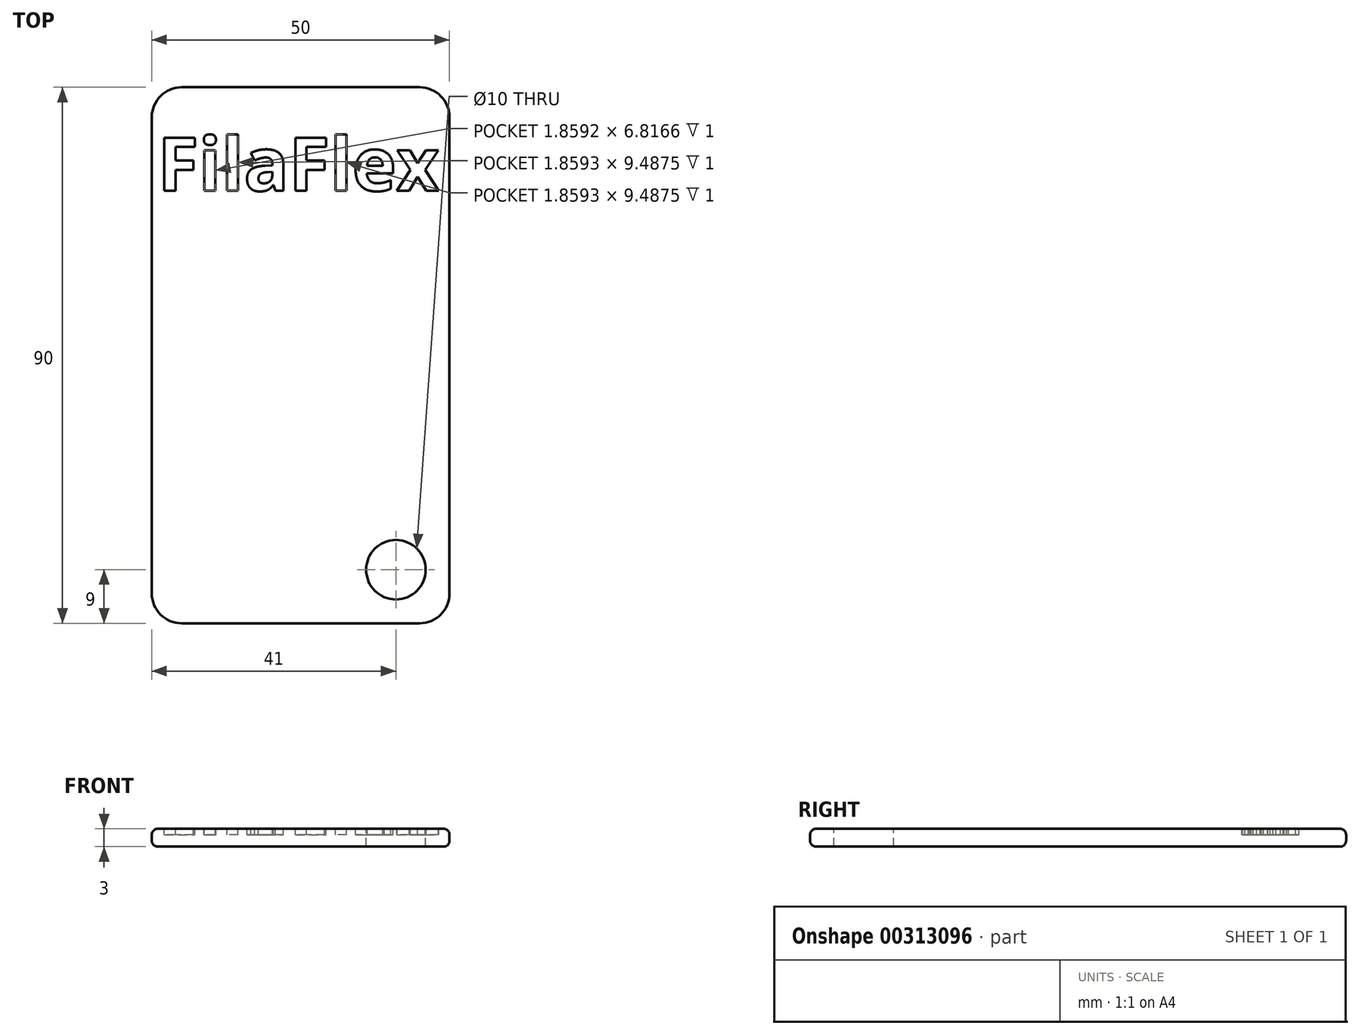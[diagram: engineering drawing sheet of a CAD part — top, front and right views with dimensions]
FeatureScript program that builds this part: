
annotation { "Feature Type Name" : "Feature", "Feature Type Description" : "" }
export const myFeature = defineFeature(function(context is Context, id is Id, definition is map)
    precondition{}
    {
        {
            var Q0;
            Q0=qCreatedBy(makeId("Top.planeOp"),FACE);
            var sketch = newSketch(context, id + "F0", { "sketchPlane" : qUnion([Q0])});
            skLineSegment(sketch, "E0.bottom", {"start": v(-45, 25) * mm, "end": v(45, 25) * mm});
            skLineSegment(sketch, "E0.top", {"start": v(-45, -25) * mm, "end": v(45, -25) * mm});
            skLineSegment(sketch, "E0.left", {"start": v(-45, 25) * mm, "end": v(-45, -25) * mm});
            skLineSegment(sketch, "E0.right", {"start": v(45, 25) * mm, "end": v(45, -25) * mm});
            skLineSegment(sketch, "E1", {"start": v(-45, 25) * mm, "end": v(45, -25) * mm, "construction": true});
            skSolve(sketch);
        }
        {
            var Q0;
            Q0=makeQuery(id+"F0.imprint","IMPRINT",FACE,{"disambiguationData":[TD([[makeQuery(id+"F0.imprint","IMPRINT",EDGE,{"derivedFrom":sQuery(id+"F0.wireOp",EDGE,"E0.bottom")}),-1.0]])]});
            extrude(context, id + "F1", {"entities" : qUnion([Q0]), "depth" : 3 * mm});
        }
        {
            var Q0;
            Q0=makeQuery(id+"F1.opExtrude","CAP_FACE",FACE,{"disambiguationData":[OSD([sQuery(id+"F0.wireOp",EDGE,"E0.bottom"),sQuery(id+"F0.wireOp",EDGE,"E0.top"),sQuery(id+"F0.wireOp",EDGE,"E0.left"),sQuery(id+"F0.wireOp",EDGE,"E0.right")])],"isStart":false});
            var Q1;
            Q1=makeQuery(id+"F1.opExtrude","CAP_FACE",FACE,{"disambiguationData":[OSD([sQuery(id+"F0.wireOp",EDGE,"E0.bottom"),sQuery(id+"F0.wireOp",EDGE,"E0.top"),sQuery(id+"F0.wireOp",EDGE,"E0.left"),sQuery(id+"F0.wireOp",EDGE,"E0.right")])],"isStart":true});
            fillet(context, id + "F2", {"entities" : qUnion([Q0, Q1]), "radius" : 1 * mm, "tangentPropagation" : true, "allowEdgeOverflow" : false});
        }
        {
            var Q0;
            Q0=makeQuery(id+"F1.opExtrude","SWEPT_EDGE",EDGE,{"disambiguationData":[OSD([sQuery(id+"F0.wireOp",EDGE,"E0.top"),sQuery(id+"F0.wireOp",EDGE,"E0.right")])]});
            var Q1;
            Q1=makeQuery(id+"F1.opExtrude","SWEPT_EDGE",EDGE,{"disambiguationData":[OSD([sQuery(id+"F0.wireOp",EDGE,"E0.bottom"),sQuery(id+"F0.wireOp",EDGE,"E0.right")])]});
            var Q2;
            Q2=makeQuery(id+"F1.opExtrude","SWEPT_EDGE",EDGE,{"disambiguationData":[OSD([sQuery(id+"F0.wireOp",EDGE,"E0.bottom"),sQuery(id+"F0.wireOp",EDGE,"E0.left")])]});
            var Q3;
            Q3=makeQuery(id+"F1.opExtrude","SWEPT_EDGE",EDGE,{"disambiguationData":[OSD([sQuery(id+"F0.wireOp",EDGE,"E0.top"),sQuery(id+"F0.wireOp",EDGE,"E0.left")])]});
            fillet(context, id + "F3", {"entities" : qUnion([Q0, Q1, Q2, Q3]), "radius" : 5 * mm, "tangentPropagation" : true, "allowEdgeOverflow" : false});
        }
        {
            var Q0;
            Q0=qCreatedBy(makeId("Right.planeOp"),FACE);
            var sketch = newSketch(context, id + "F4", { "sketchPlane" : qUnion([Q0])});
            skLineSegment(sketch, "E2", {"start": v(0, 0) * mm, "end": v(0, 32.9) * mm});
            skSolve(sketch);
        }
        {
            var Q0;
            Q0=makeQuery(id+"F1.opExtrude","SWEPT_BODY",BODY,{"disambiguationData":[OSD([sQuery(id+"F0.wireOp",EDGE,"E0.bottom"),sQuery(id+"F0.wireOp",EDGE,"E0.top"),sQuery(id+"F0.wireOp",EDGE,"E0.left"),sQuery(id+"F0.wireOp",EDGE,"E0.right")])]});
            var Q1;
            Q1=sQuery(id+"F4.wireOp",EDGE,"E2");
            transform(context, id + "F5", {"entities" : qUnion([Q0]), "transformType" : TransformType.ROTATION, "transformAxis" : qUnion([Q1]), "angle" : 90 * degree, "makeCopy" : false});
        }
        {
            var Q0;
            Q0=makeQuery(id+"F1.opExtrude","CAP_FACE",FACE,{"disambiguationData":[OSD([sQuery(id+"F0.wireOp",EDGE,"E0.bottom"),sQuery(id+"F0.wireOp",EDGE,"E0.top"),sQuery(id+"F0.wireOp",EDGE,"E0.left"),sQuery(id+"F0.wireOp",EDGE,"E0.right")])],"isStart":false});
            var sketch = newSketch(context, id + "F6", { "sketchPlane" : qUnion([Q0])});
            skText(sketch, "E3", { "text": "FilaFlex\n", "fontName": "OpenSans-Bold.ttf"});
            const initialGuessF6  = {"E3": [-0.024, 0.02763, 1, 0, 0.00899]};
            skSetInitialGuess(sketch, initialGuessF6);
            skSolve(sketch);
        }
        {
            var Q0;
            Q0=qSketchRegion(id+"F6",true);
            extrude(context, id + "F7", {"entities" : qUnion([Q0]), "operationType" : NewBodyOperationType.REMOVE, "oppositeDirection" : true, "depth" : 1 * mm});
        }
        {
            var Q0;
            {var subQ0=sQuery(id+"F0.wireOp",EDGE,"E0.left");var subQ2=sQuery(id+"F0.wireOp",EDGE,"E0.bottom");var subQ4=sQuery(id+"F0.wireOp",EDGE,"E0.right");var subQ6=sQuery(id+"F0.wireOp",EDGE,"E0.top");Q0=makeQuery(id+"F7.boolean.opBoolean","SPLIT",FACE,{"disambiguationData":[TD([makeQuery(id+"F7.opExtrude","SWEPT_FACE",FACE,{"disambiguationData":[OSD([sQuery(id+"F6.wireOp",EDGE,"E3.sketch_text.stroke-0")])]})])],"derivedFrom":makeQuery(id+"F1.opExtrude","CAP_FACE",FACE,{"disambiguationData":[OSD([subQ2,subQ6,subQ0,subQ4])],"isStart":false})});}
            var sketch = newSketch(context, id + "F8", { "sketchPlane" : qUnion([Q0])});
            skCircle(sketch, "E4", {"center": v(16, -36) * mm, "radius": 5 * mm});
            skSolve(sketch);
        }
        {
            var Q0;
            Q0=qSketchRegion(id+"F8",true);
            extrude(context, id + "F9", {"entities" : qUnion([Q0]), "operationType" : NewBodyOperationType.REMOVE, "oppositeDirection" : true, "depth" : 3 * mm});
        }
    });
